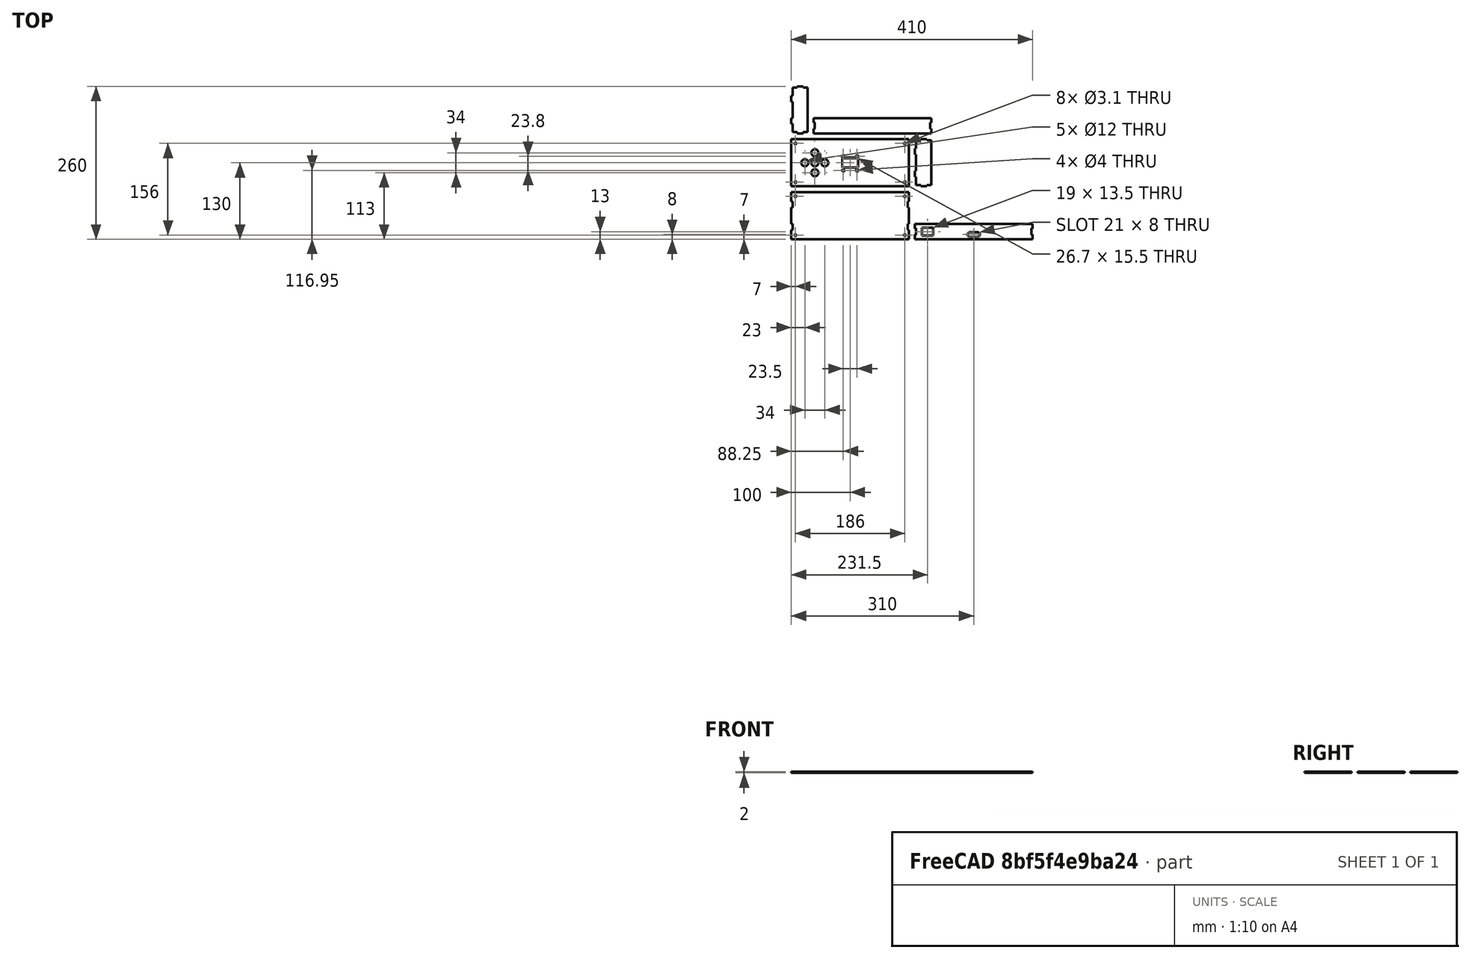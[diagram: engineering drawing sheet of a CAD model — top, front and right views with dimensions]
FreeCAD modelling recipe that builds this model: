
FCSTD DOCUMENT  (FreeCAD 1.0R39109 (Git))
Label: export_shape2
License: All rights reserved
LicenseURL: http://en.wikipedia.org/wiki/All_rights_reserved
objects: Part::Feature×6, Part::Part2DObjectPython×6
note: 12 computed .brp shape members not serialized (recipe doc carries the construction recipe); baked Part::Feature solids carry a one-line shape summary decoded from their .brp

FEATURE [Part::Feature] test
  Placement = pos=(100,40,17) rot=(0,-1,0;3.14159rad)
  shape: bbox 200 x 80 x 2 mm, 34 faces (baked)
FEATURE [Part::Feature] test001
  Placement = pos=(310,13,70) rot=(-1,0,0;1.5708rad)
  shape: bbox 200 x 26 x 2 mm, 26 faces (baked)
FEATURE [Part::Feature] test002
  Placement = pos=(100,130,45) rot=(0,-1,0;3.14159rad)
  shape: bbox 200 x 80 x 2 mm, 23 faces (baked)
FEATURE [Part::Feature] test003
  Placement = pos=(225,130,-68) rot=(0,1,0;1.5708rad)
  shape: bbox 28 x 80 x 2 mm, 22 faces (baked)
FEATURE [Part::Feature] test004
  Placement = pos=(15,220,130) rot=(0,1,0;1.5708rad)
  shape: bbox 28 x 80 x 2 mm, 22 faces (baked)
FEATURE [Part::Feature] test005
  Placement = pos=(138,193,-8) rot=(-1,0,0;1.5708rad)
  shape: bbox 200 x 26 x 2 mm, 18 faces (baked)
FEATURE [Part::Part2DObjectPython] Shape2DView  # Draft 2D object (typed FeaturePython)
  AutoUpdate = true
  Base = -> test
  Clip = false
  FuseArch = false
  HiddenLines = false
  InPlace = true
  OnlySolids = false
  Projection = (0,0,1)
  ProjectionMode = 0
  SegmentLength = 0.05
  Tessellation = false
  VisibleOnly = false
FEATURE [Part::Part2DObjectPython] Shape2DView001  # Draft 2D object (typed FeaturePython)
  AutoUpdate = true
  Base = -> test001
  Clip = false
  FuseArch = false
  HiddenLines = false
  InPlace = true
  OnlySolids = false
  Placement = pos=(-210,-40,0) rot=(0,0,1;0rad)
  Projection = (0,0,1)
  ProjectionMode = 0
  SegmentLength = 0.05
  Tessellation = false
  VisibleOnly = false
FEATURE [Part::Part2DObjectPython] Shape2DView002  # Draft 2D object (typed FeaturePython)
  AutoUpdate = true
  Base = -> test002
  Clip = false
  FuseArch = false
  HiddenLines = false
  InPlace = true
  OnlySolids = false
  Projection = (0,0,1)
  ProjectionMode = 0
  SegmentLength = 0.05
  Tessellation = false
  VisibleOnly = false
FEATURE [Part::Part2DObjectPython] Shape2DView003  # Draft 2D object (typed FeaturePython)
  AutoUpdate = true
  Base = -> test003
  Clip = false
  FuseArch = false
  HiddenLines = false
  InPlace = true
  OnlySolids = false
  Placement = pos=(268,-290,0) rot=(0,0,1;1.5708rad)
  Projection = (0,0,1)
  ProjectionMode = 0
  SegmentLength = 0.05
  Tessellation = false
  VisibleOnly = false
FEATURE [Part::Part2DObjectPython] Shape2DView004  # Draft 2D object (typed FeaturePython)
  AutoUpdate = true
  Base = -> test004
  Clip = false
  FuseArch = false
  HiddenLines = false
  InPlace = true
  OnlySolids = false
  Placement = pos=(265,-80,0) rot=(0,0,1;1.5708rad)
  Projection = (0,0,1)
  ProjectionMode = 0
  SegmentLength = 0.05
  Tessellation = false
  VisibleOnly = false
FEATURE [Part::Part2DObjectPython] Shape2DView005  # Draft 2D object (typed FeaturePython)
  AutoUpdate = true
  Base = -> test005
  Clip = false
  FuseArch = false
  HiddenLines = false
  InPlace = true
  OnlySolids = false
  Placement = pos=(-40,-300,0) rot=(0,0,1;0rad)
  Projection = (0,0,1)
  ProjectionMode = 0
  SegmentLength = 0.05
  Tessellation = false
  VisibleOnly = false
